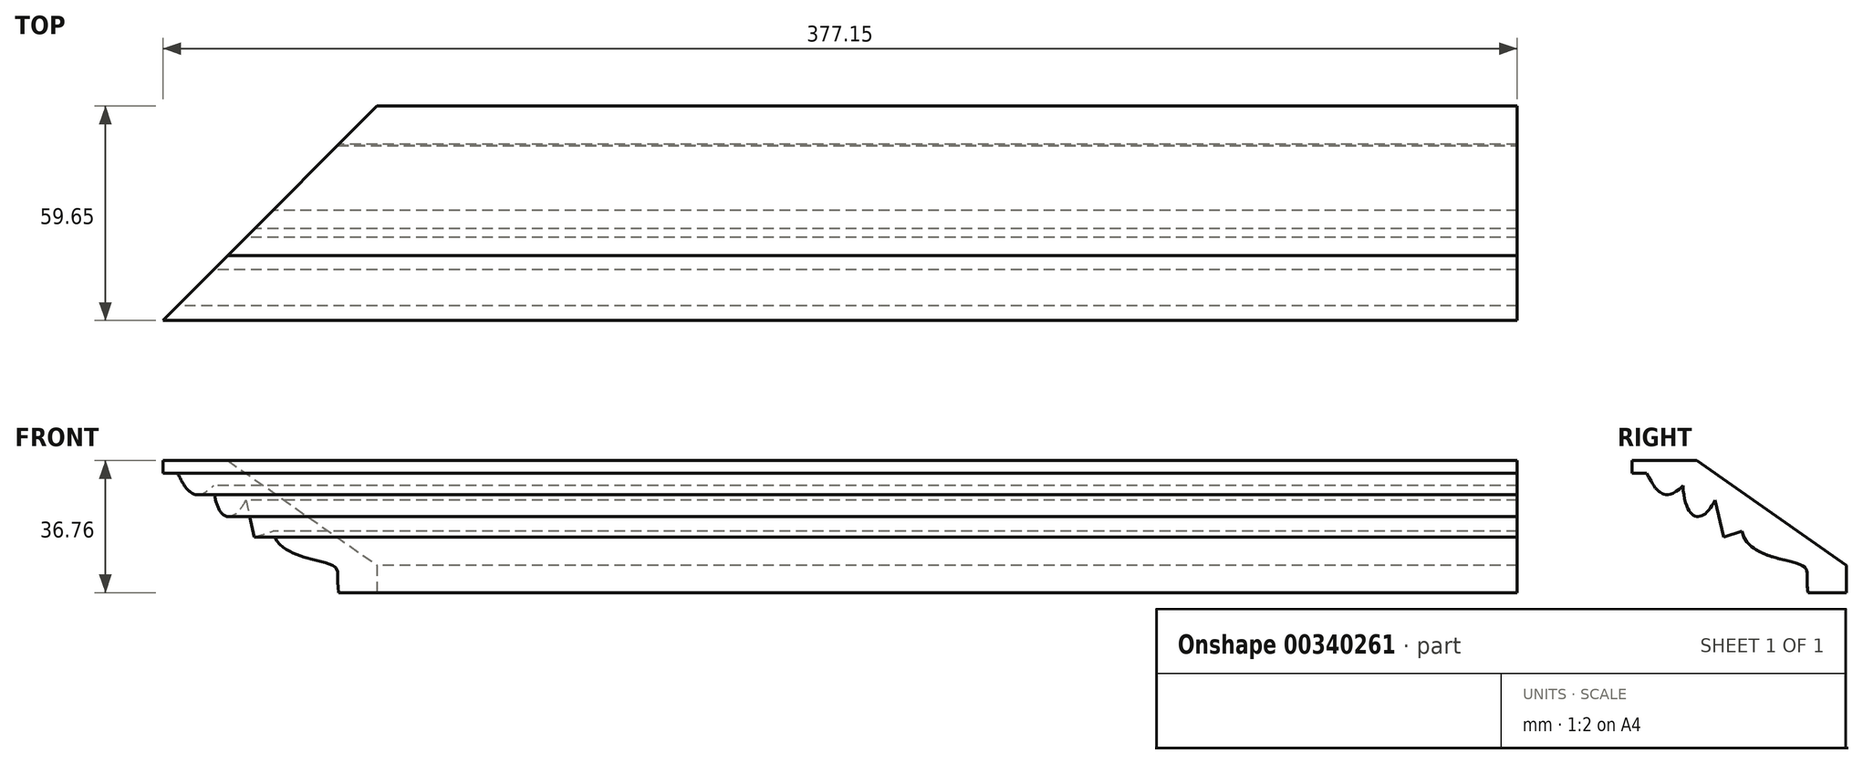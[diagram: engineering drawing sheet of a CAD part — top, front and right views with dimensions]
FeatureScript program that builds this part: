
annotation { "Feature Type Name" : "Feature", "Feature Type Description" : "" }
export const myFeature = defineFeature(function(context is Context, id is Id, definition is map)
    precondition{}
    {
        {
            var Q0;
            Q0=qCreatedBy(makeId("Right.planeOp"),FACE);
            var sketch = newSketch(context, id + "F0", { "sketchPlane" : qUnion([Q0])});
            skLineSegment(sketch, "E0", {"start": v(0, 7.62) * mm, "end": v(-41.61, 36.76) * mm});
            skLineSegment(sketch, "E1", {"start": v(-41.61, 36.76) * mm, "end": v(-59.65, 36.76) * mm});
            skLineSegment(sketch, "E2", {"start": v(-59.65, 36.76) * mm, "end": v(-59.65, 33.27) * mm});
            skLineSegment(sketch, "E3", {"start": v(-59.65, 33.27) * mm, "end": v(-55.58, 33.27) * mm});
            skLineSegment(sketch, "E4", {"start": v(0, 7.62) * mm, "end": v(0, 0) * mm});
            skLineSegment(sketch, "E5", {"start": v(0, 0) * mm, "end": v(-10.67, 0) * mm});
            skFitSpline(sketch, "E6", {"points": [v(-10.67, 0) * mm, v(-11.01, 5.96) * mm, v(-13.27, 7.99) * mm, v(-29.01, 17.09) * mm], "startDerivative": vector(-5.08, 29.03) * mm, "endDerivative": vector(-6.54, 39.72) * mm});
            skLineSegment(sketch, "E7", {"start": v(-29.01, 17.09) * mm, "end": v(-34.16, 15.48) * mm});
            skLineSegment(sketch, "E8", {"start": v(-34.16, 15.48) * mm, "end": v(-36.54, 25.8) * mm});
            skFitSpline(sketch, "E9", {"points": [v(-45.51, 29.77) * mm, v(-52.42, 28.4) * mm, v(-55.58, 33.27) * mm], "startDerivative": vector(-24.15, -24.15) * mm, "endDerivative": vector(-16.65, 31.11) * mm});
            skFitSpline(sketch, "E10", {"points": [v(-45.51, 29.77) * mm, v(-36.54, 25.8) * mm], "startDerivative": vector(2.07, -32.09) * mm, "endDerivative": vector(9.32, 20.18) * mm});
            skSolve(sketch);
        }
        {
            var Q0;
            Q0 = qSketchRegion(id + "F0", true);
            extrude(context, id + "F1", {"entities" : qUnion([Q0]), "depth" : 228.6 * mm, "hasSecondDirection" : true, "secondDirectionOppositeDirection" : true, "secondDirectionDepth" : 177.8 * mm});
        }
        {
            var Q0;
            Q0=qCreatedBy(makeId("Top.planeOp"),FACE);
            var sketch = newSketch(context, id + "F2", { "sketchPlane" : qUnion([Q0])});
            skLineSegment(sketch, "E11", {"start": v(-88.9, 0) * mm, "end": v(88.9, 0) * mm, "construction": true});
            skLineSegment(sketch, "E12", {"start": v(0, 0) * mm, "end": v(0, -141.75) * mm, "construction": true});
            skLineSegment(sketch, "E13.MirrorCS", {"start": v(-88.9, 0) * mm, "end": v(-192.6, 0) * mm});
            skLineSegment(sketch, "E14.MirrorCS", {"start": v(-192.6, -103.7) * mm, "end": v(-88.9, 0) * mm});
            skLineSegment(sketch, "E15.MirrorCS", {"start": v(-192.6, 0) * mm, "end": v(-192.6, -103.7) * mm});
            skSolve(sketch);
        }
        {
            var Q0;
            Q0 = qSketchRegion(id + "F2", true);
            extrude(context, id + "F3", {"entities" : qUnion([Q0]), "operationType" : NewBodyOperationType.REMOVE, "endBound" : BoundingType.THROUGH_ALL, "depth" : 25.4 * mm});
        }
    });
